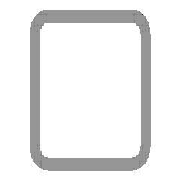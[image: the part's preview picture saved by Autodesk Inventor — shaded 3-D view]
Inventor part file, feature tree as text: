
AUTODESK INVENTOR PART (.ipt)
format: ipt  version: 2025.1 (Build 291241020, 241B)  size: 136,704 bytes
history: native  units: mm (DEFAULTED — no unit token found)
features: other x4, sketch x1, plane x1
ambient origin geometry x8: Origin, YZ Plane, XZ Plane, XY Plane, X Axis, Y Axis, Z Axis, Center Point
bodies: Solid1 (feature_tree), Body (feature_tree)
feature tree (6):
  parser-record x1  (decoder bookkeeping rows leaked as tree rows — omitted from the tree; the rows remain in map.json)
  other  "Driven Length"
  other  "Start plane"
  other  "End plane"
  sketch  "Sketch3"  dims[d3=1050.0mm d4=0.0mm d7=6.0mm d9=100.0mm d11=100.0mm d12=3.0mm d13=50.0mm d14=1100.0mm d15=50.0mm d16=50.0mm d17=90.0deg d18=1050.0mm]
  plane  "Work Plane3"
